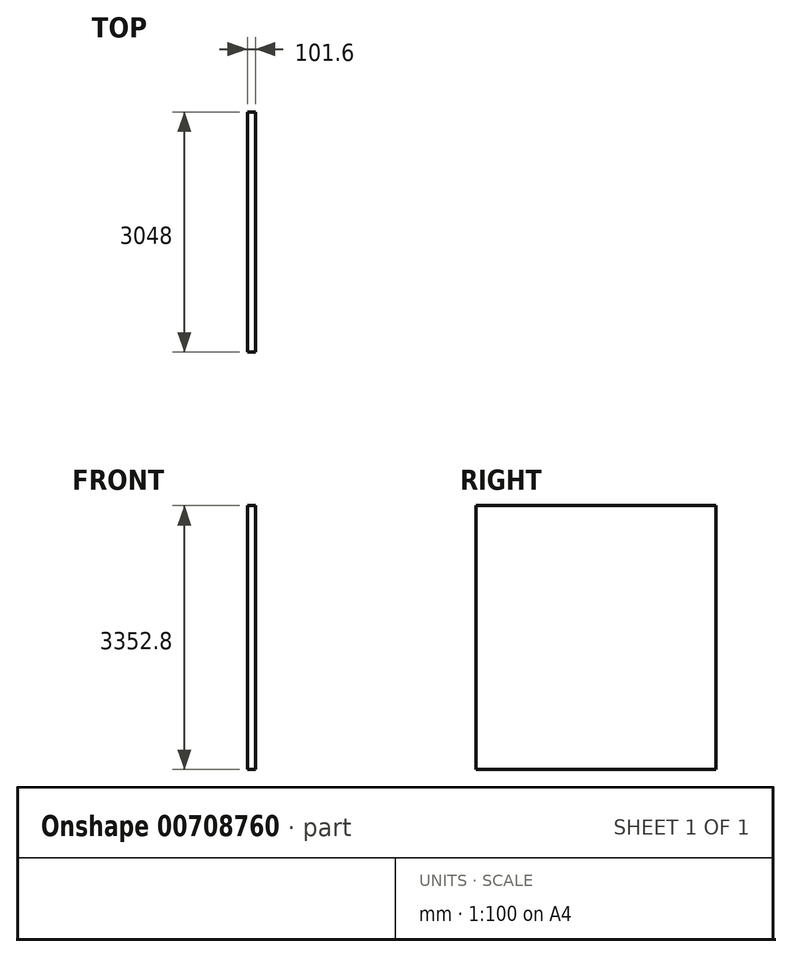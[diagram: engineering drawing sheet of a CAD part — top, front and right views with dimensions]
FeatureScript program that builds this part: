
annotation { "Feature Type Name" : "Feature", "Feature Type Description" : "" }
export const myFeature = defineFeature(function(context is Context, id is Id, definition is map)
    precondition{}
    {
        {
            var Q0;
            Q0=qCreatedBy(makeId("Front.planeOp"),FACE);
            var sketch = newSketch(context, id + "F0", { "sketchPlane" : qUnion([Q0])});
            skLineSegment(sketch, "E0", {"start": v(0, 0) * mm, "end": v(0, 3352.8) * mm});
            skLineSegment(sketch, "E1", {"start": v(0, 3352.8) * mm, "end": v(101.6, 3352.8) * mm});
            skLineSegment(sketch, "E2", {"start": v(101.6, 3352.8) * mm, "end": v(101.6, 0) * mm});
            skLineSegment(sketch, "E3", {"start": v(101.6, 0) * mm, "end": v(0, 0) * mm});
            skSolve(sketch);
        }
        {
            var Q0;
            Q0 = qSketchRegion(id + "F0", true);
            extrude(context, id + "F1", {"entities" : qUnion([Q0]), "depth" : 3048 * mm, "offsetDistance" : 25.4 * mm});
        }
    });
